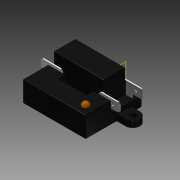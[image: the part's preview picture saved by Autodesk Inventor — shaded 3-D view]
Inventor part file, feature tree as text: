
AUTODESK INVENTOR PART (.ipt)
format: ipt  version: 2013 (Build 170138000, 138)  size: 403,456 bytes
history: native  units: mm (DEFAULTED — no unit token found)
features: sketch x3, fillet x2, plane x2, extrude x2, other x1, hole x1, mirror x1, imported_body x1
ambient origin geometry x8: Origin, YZ Plane, XZ Plane, XY Plane, X Axis, Y Axis, Z Axis, Center Point
bodies: Solid1 (feature_tree)
feature tree (13):
  other  "Spike Relay.ipt"
  fillet  "Fillet1"  Radius=0.762mm
  sketch  "Sketch2"  dims[d14=13.208mm d15=29.083mm]
  plane  "Work Plane1"
  extrude  "Extrusion1"  Depth=29.083mm
  extrude  "Extrusion2"  Depth=25.4mm TaperAngle=0.0deg
  hole  "Hole1"  [1 undecoded]
  plane  "Work Plane2"
  mirror  "Mirror2"
  fillet  "Fillet2"  [1 undecoded]
  imported_body  "DerivedBody::Spike Relay.ipt"
  sketch  "Sketch3"  dims[d16=34.0868mm d17=-4.318mm d18=25.4mm d19=0.0mm]
  sketch  "Sketch4"  dims[d20=25.4mm d21=0.0mm d22=4.4958mm d23=19.05mm d24=8.4328mm d25=6.35mm d26=14.3117mm d27=25.4mm d28=20.594885mm d29=0.635mm]
note: 2 required parameter values undecoded (feature->parameter linkage not recoverable at this tier; creation-order binding heuristic only, values carry confidence <= 0.55)
